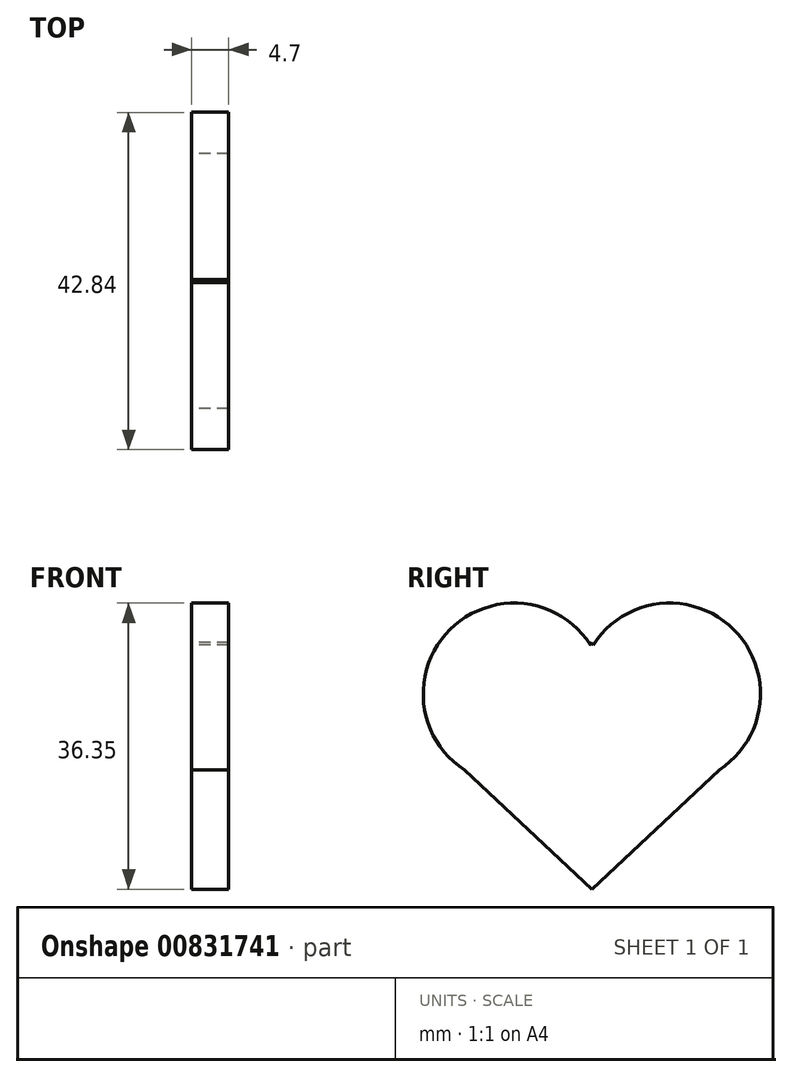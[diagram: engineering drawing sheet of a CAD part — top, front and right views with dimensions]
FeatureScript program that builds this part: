
annotation { "Feature Type Name" : "Feature", "Feature Type Description" : "" }
export const myFeature = defineFeature(function(context is Context, id is Id, definition is map)
    precondition{}
    {
        {
            var Q0;
            Q0=qCreatedBy(makeId("Right.planeOp"),FACE);
            var sketch = newSketch(context, id + "F0", { "sketchPlane" : qUnion([Q0])});
            skArc(sketch, "E0", {"start": v(-1.33, 9.04) * mm, "mid": v(-19.21, 11.28) * mm, "end": v(-17.46, -6.65) * mm});
            skArc(sketch, "E1.1.0", {"start": v(14.95, -6.14) * mm, "mid": v(16.37, 11.82) * mm, "end": v(-1.46, 9.25) * mm});
            skPoint(sketch, "E1.center", {"position": v(-11.17, -16.9) * mm});
            skFitSpline(sketch, "E2", {"points": [v(-17.46, -6.65) * mm, v(-1.29, -21.8) * mm], "startDerivative": vector(16.18, -15.15) * mm, "endDerivative": vector(16.18, -15.15) * mm});
            skFitSpline(sketch, "E3", {"points": [v(14.95, -6.4) * mm, v(-1.29, -21.8) * mm], "startDerivative": vector(-16.21, -15.44) * mm, "endDerivative": vector(-16.21, -15.44) * mm});
            skArc(sketch, "E4.MirrorCS", {"start": v(-17.52, -6.14) * mm, "mid": v(-18.94, 11.82) * mm, "end": v(-1.1, 9.25) * mm});
            skFitSpline(sketch, "E5.MirrorCS", {"points": [v(14.9, -6.65) * mm, v(-1.29, -21.8) * mm], "startDerivative": vector(-16.18, -15.15) * mm, "endDerivative": vector(-16.18, -15.15) * mm});
            skArc(sketch, "E6.MirrorCS", {"start": v(-1.24, 9.04) * mm, "mid": v(16.64, 11.28) * mm, "end": v(14.9, -6.65) * mm});
            skSolve(sketch);
        }
        {
            var Q0;
            {var subQ5=sQuery(id+"F0.wireOp",EDGE,"E2");Q0=makeQuery(id+"F0.imprint","IMPRINT",FACE,{"disambiguationData":[TD([[makeQuery(id+"F0.imprint","IMPRINT",EDGE,{"derivedFrom":subQ5}),1.0]])]});}
            extrude(context, id + "F1", {"entities" : qUnion([Q0]), "depth" : 4.7 * mm, "offsetDistance" : 25 * mm});
        }
    });
